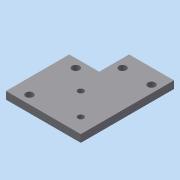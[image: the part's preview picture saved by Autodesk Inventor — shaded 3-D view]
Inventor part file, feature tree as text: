
AUTODESK INVENTOR PART (.ipt)
format: ipt  version: 2015 (Build 190159000, 159)  size: 99,328 bytes
history: native  units: mm
features: sketch x4, other x3
ambient origin geometry x8: Origin, YZ Plane, XZ Plane, XY Plane, X Axis, Y Axis, Z Axis, Center Point
bodies: Solid1 (feature_tree)
feature tree (7):
  other  "Corner mount.ipt"
  other  "Solid1::Corner mount.ipt"
  other  "TaggingFeature1"
  sketch  "Sketch1"  dims[d0=10.0mm]
  sketch  "Sketch2"
  sketch  "Sketch3"
  sketch  "Sketch4"
